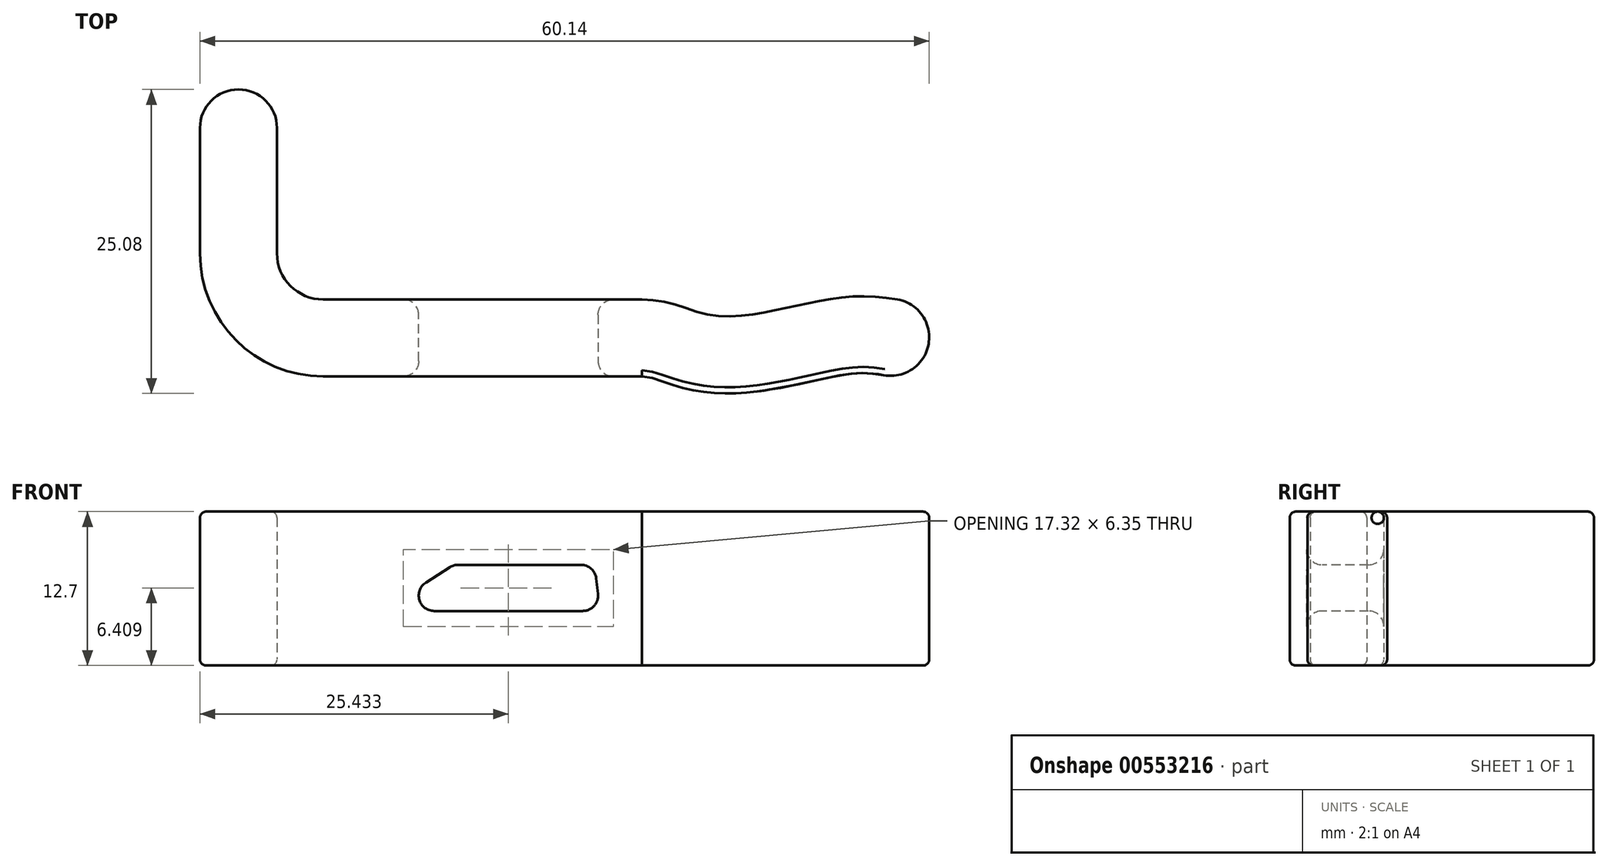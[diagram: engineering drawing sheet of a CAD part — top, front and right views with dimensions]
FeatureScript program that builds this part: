
annotation { "Feature Type Name" : "Feature", "Feature Type Description" : "" }
export const myFeature = defineFeature(function(context is Context, id is Id, definition is map)
    precondition{}
    {
        {
            var Q0;
            Q0=qCreatedBy(makeId("Top.planeOp"),FACE);
            var sketch = newSketch(context, id + "F0", { "sketchPlane" : qUnion([Q0])});
            skLineSegment(sketch, "E0", {"start": v(0, 0) * mm, "end": v(0, -10.34) * mm});
            skLineSegment(sketch, "E1", {"start": v(3.8, -14.15) * mm, "end": v(30.1, -14.15) * mm});
            skFitSpline(sketch, "E2", {"points": [v(30.1, -14.15) * mm, v(36.32, -15.52) * mm, v(45.43, -14.15) * mm, v(51.17, -14.15) * mm], "startDerivative": vector(25.88, 0) * mm, "endDerivative": vector(18.6, -3.32) * mm});
            skPoint(sketch, "E3.visualSharp", {"position": v(0, -14.15) * mm});
            skArc(sketch, "E3.filletArc", {"start": v(0, -10.34) * mm, "mid": v(1.12, -13.04) * mm, "end": v(3.81, -14.15) * mm});
            skFitSpline(sketch, "E4.0", {"points": [v(30.1, -20.5) * mm, v(30.28, -20.5) * mm, v(30.52, -20.53) * mm, v(30.86, -20.6) * mm, v(31.35, -20.76) * mm, v(31.85, -20.93) * mm, v(32.51, -21.16) * mm, v(33.34, -21.41) * mm, v(34.18, -21.62) * mm, v(34.93, -21.75) * mm, v(35.42, -21.82) * mm, v(35.83, -21.86) * mm, v(36.23, -21.89) * mm, v(36.72, -21.9) * mm, v(37.29, -21.9) * mm, v(38.02, -21.89) * mm, v(38.9, -21.82) * mm, v(39.9, -21.7) * mm, v(40.86, -21.55) * mm, v(42.09, -21.33) * mm, v(43.53, -21.03) * mm, v(45.07, -20.69) * mm, v(46.15, -20.47) * mm, v(46.81, -20.36) * mm, v(47.26, -20.3) * mm, v(47.65, -20.26) * mm, v(48.13, -20.23) * mm, v(48.66, -20.23) * mm, v(49.3, -20.28) * mm, v(49.78, -20.35) * mm, v(50.06, -20.4) * mm]});
            skLineSegment(sketch, "E4.1", {"start": v(3.8, -20.5) * mm, "end": v(30.1, -20.5) * mm});
            skArc(sketch, "E4.2", {"start": v(-6.35, -10.34) * mm, "mid": v(-3.37, -17.53) * mm, "end": v(3.8, -20.5) * mm});
            skLineSegment(sketch, "E4.3", {"start": v(-6.35, 0) * mm, "end": v(-6.35, -10.34) * mm});
            skLineSegment(sketch, "E5", {"start": v(-6.35, 0) * mm, "end": v(0, 0) * mm, "construction": true});
            skLineSegment(sketch, "E6", {"start": v(51.17, -14.15) * mm, "end": v(50.06, -20.4) * mm, "construction": true});
            skCircle(sketch, "E7", {"center": v(-3.17, 0) * mm, "radius": 3.17 * mm});
            skCircle(sketch, "E8", {"center": v(50.61, -17.28) * mm, "radius": 3.17 * mm});
            skSolve(sketch);
        }
        {
            var Q0;
            Q0 = qSketchRegion(id + "F0", true);
            extrude(context, id + "F1", {"entities" : qUnion([Q0]), "depth" : 12.7 * mm, "offsetDistance" : 25.4 * mm});
        }
        {
            var Q0;
            Q0=makeQuery(id+"F1.opExtrude","SWEPT_FACE",FACE,{"disambiguationData":[OSD([sQuery(id+"F0.wireOp",EDGE,"E4.2")])]});
            var Q1;
            Q1=makeQuery(id+"F1.opExtrude","CAP_FACE",FACE,{"disambiguationData":[OSD([sQuery(id+"F0.wireOp",EDGE,"E0"),sQuery(id+"F0.wireOp",EDGE,"E1"),sQuery(id+"F0.wireOp",EDGE,"E2"),sQuery(id+"F0.wireOp",EDGE,"E3.filletArc"),sQuery(id+"F0.wireOp",EDGE,"E4.0"),sQuery(id+"F0.wireOp",EDGE,"E4.1"),sQuery(id+"F0.wireOp",EDGE,"E4.2"),sQuery(id+"F0.wireOp",EDGE,"E4.3"),sQuery(id+"F0.wireOp",EDGE,"E7"),sQuery(id+"F0.wireOp",EDGE,"E8")])],"isStart":false});
            fillet(context, id + "F2", {"entities" : qUnion([Q0, Q1]), "radius" : 0.5 * mm, "tangentPropagation" : true, "allowEdgeOverflow" : false});
        }
        {
            var Q0;
            Q0=makeQuery(id+"F1.opExtrude","SWEPT_FACE",FACE,{"disambiguationData":[OSD([sQuery(id+"F0.wireOp",EDGE,"E4.1")])]});
            var sketch = newSketch(context, id + "F3", { "sketchPlane" : qUnion([Q0])});
            skLineSegment(sketch, "E9", {"start": v(14.58, 8.31) * mm, "end": v(26.2, 8.31) * mm});
            skLineSegment(sketch, "E10.0", {"start": v(8.61, 4.5) * mm, "end": v(26.64, 4.5) * mm});
            skLineSegment(sketch, "E11", {"start": v(14.58, 8.31) * mm, "end": v(8.61, 4.5) * mm});
            skLineSegment(sketch, "E12", {"start": v(26.2, 8.31) * mm, "end": v(26.64, 4.5) * mm});
            skSolve(sketch);
        }
        {
            var Q0;
            Q0 = qSketchRegion(id + "F3", true);
            var Q1;
            Q1=sQuery(id+"F3.wireOp",EDGE,"E11");
            var Q2;
            Q2=sQuery(id+"F3.wireOp",EDGE,"E9");
            extrude(context, id + "F4", {"entities" : qUnion([Q0]), "operationType" : NewBodyOperationType.REMOVE, "surfaceEntities" : qUnion([Q1, Q2]), "endBound" : BoundingType.THROUGH_ALL, "oppositeDirection" : true, "depth" : 25.4 * mm, "offsetDistance" : 25.4 * mm});
        }
        {
            var Q0;
            Q0=makeQuery(id+"F4.boolean.opBoolean","COPY",EDGE,{"derivedFrom":makeQuery(id+"F4.opExtrude","SWEPT_EDGE",EDGE,{"disambiguationData":[OSD([sQuery(id+"F3.wireOp",EDGE,"E10.0"),sQuery(id+"F3.wireOp",EDGE,"E11")])]})});
            var Q1;
            Q1=makeQuery(id+"F4.boolean.opBoolean","COPY",EDGE,{"derivedFrom":makeQuery(id+"F4.opExtrude","SWEPT_EDGE",EDGE,{"disambiguationData":[OSD([sQuery(id+"F3.wireOp",EDGE,"E9"),sQuery(id+"F3.wireOp",EDGE,"E12")])]})});
            var Q2;
            Q2=makeQuery(id+"F4.boolean.opBoolean","COPY",EDGE,{"derivedFrom":makeQuery(id+"F4.opExtrude","SWEPT_EDGE",EDGE,{"disambiguationData":[OSD([sQuery(id+"F3.wireOp",EDGE,"E9"),sQuery(id+"F3.wireOp",EDGE,"E11")])]})});
            var Q3;
            Q3=makeQuery(id+"F4.boolean.opBoolean","COPY",EDGE,{"derivedFrom":makeQuery(id+"F4.opExtrude","SWEPT_EDGE",EDGE,{"disambiguationData":[OSD([sQuery(id+"F3.wireOp",EDGE,"E10.0"),sQuery(id+"F3.wireOp",EDGE,"E12")])]})});
            fillet(context, id + "F5", {"entities" : qUnion([Q0, Q1, Q2, Q3]), "radius" : 1.27 * mm, "tangentPropagation" : true, "allowEdgeOverflow" : false});
        }
        {
            var Q0;
            Q0=makeQuery(id+"F4.boolean.opBoolean","COPY",FACE,{"derivedFrom":makeQuery(id+"F4.opExtrude","SWEPT_FACE",FACE,{"disambiguationData":[OSD([sQuery(id+"F3.wireOp",EDGE,"E10.0")])]})});
            fillet(context, id + "F6", {"entities" : qUnion([Q0]), "radius" : 1.27 * mm, "tangentPropagation" : true, "allowEdgeOverflow" : false});
        }
    });
